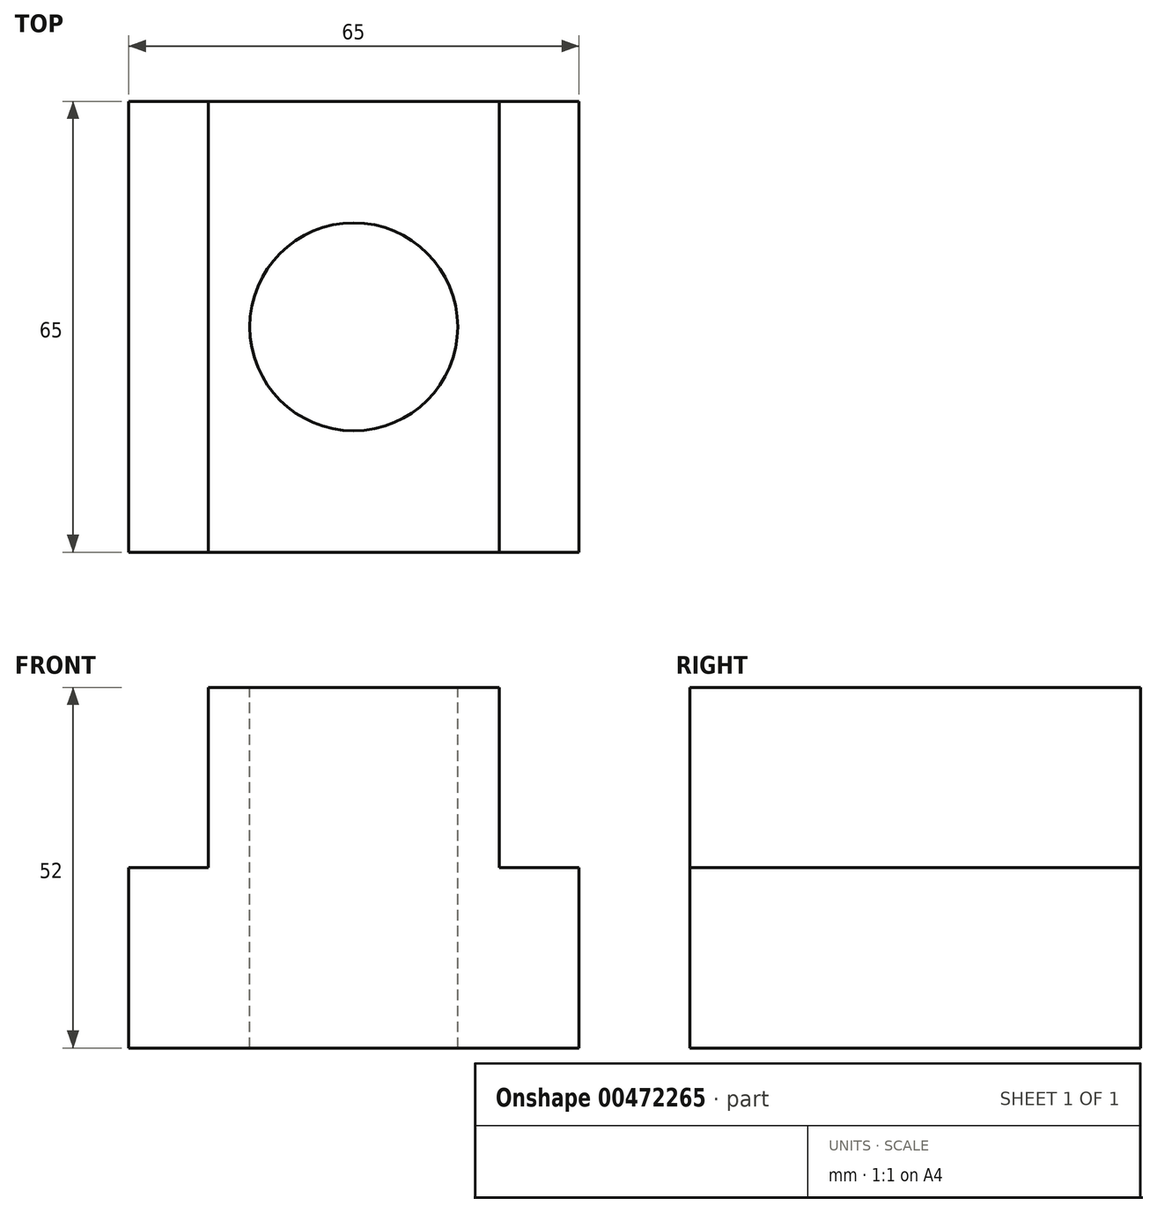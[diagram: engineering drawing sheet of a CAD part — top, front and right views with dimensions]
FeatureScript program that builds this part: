
annotation { "Feature Type Name" : "Feature", "Feature Type Description" : "" }
export const myFeature = defineFeature(function(context is Context, id is Id, definition is map)
    precondition{}
    {
        {
            var Q0;
            Q0=qCreatedBy(makeId("Front.planeOp"),FACE);
            var sketch = newSketch(context, id + "F0", { "sketchPlane" : qUnion([Q0])});
            skLineSegment(sketch, "E0.bottom", {"start": v(32.5, -13) * mm, "end": v(-32.5, -13) * mm});
            skLineSegment(sketch, "E0.top", {"start": v(32.5, 13) * mm, "end": v(21, 13) * mm});
            skLineSegment(sketch, "E0.left", {"start": v(32.5, -13) * mm, "end": v(32.5, 13) * mm});
            skLineSegment(sketch, "E0.right", {"start": v(-32.5, -13) * mm, "end": v(-32.5, 13) * mm});
            skPoint(sketch, "E0.middle", {"position": v(0, 0) * mm});
            skLineSegment(sketch, "E1.top", {"start": v(21, 39) * mm, "end": v(-21, 39) * mm});
            skLineSegment(sketch, "E1.left", {"start": v(21, 13) * mm, "end": v(21, 39) * mm});
            skLineSegment(sketch, "E1.right", {"start": v(-21, 13) * mm, "end": v(-21, 39) * mm});
            skPoint(sketch, "E1.middle", {"position": v(0, 26) * mm});
            skLineSegment(sketch, "E2.trimOffspring", {"start": v(-21, 13) * mm, "end": v(-32.5, 13) * mm});
            skSolve(sketch);
        }
        {
            var Q0;
            Q0 = qSketchRegion(id + "F0", true);
            extrude(context, id + "F1", {"entities" : qUnion([Q0]), "depth" : 65 * mm});
        }
        {
            var Q0;
            Q0=makeQuery(id+"F1.opExtrude","SWEPT_FACE",FACE,{"disambiguationData":[OSD([sQuery(id+"F0.wireOp",EDGE,"E1.top")])]});
            var sketch = newSketch(context, id + "F2", { "sketchPlane" : qUnion([Q0])});
            skCircle(sketch, "E3", {"center": v(0, -32.5) * mm, "radius": 15 * mm});
            skSolve(sketch);
        }
        {
            var Q0;
            Q0=sQuery(id+"F2.wireOp",VERTEX,"E3.center");
            var Q1;
            Q1=makeQuery(id+"F1.opExtrude","SWEPT_BODY",BODY,{"disambiguationData":[OSD([sQuery(id+"F0.wireOp",EDGE,"E0.bottom"),sQuery(id+"F0.wireOp",EDGE,"E0.top"),sQuery(id+"F0.wireOp",EDGE,"E0.left"),sQuery(id+"F0.wireOp",EDGE,"E0.right"),sQuery(id+"F0.wireOp",EDGE,"E1.top"),sQuery(id+"F0.wireOp",EDGE,"E1.left"),sQuery(id+"F0.wireOp",EDGE,"E1.right"),sQuery(id+"F0.wireOp",EDGE,"E2.trimOffspring")])]});
            hole(context, id + "F3", {"style" : HoleStyle.SIMPLE, "endStyle" : HoleEndStyle.THROUGH, "holeDiameter" : 30 * mm, "isTappedThrough" : true, "tappedDepth" : 12 * mm, "tapClearance" : 3, "locations" : qUnion([Q0]), "scope" : qUnion([Q1])});
        }
    });
